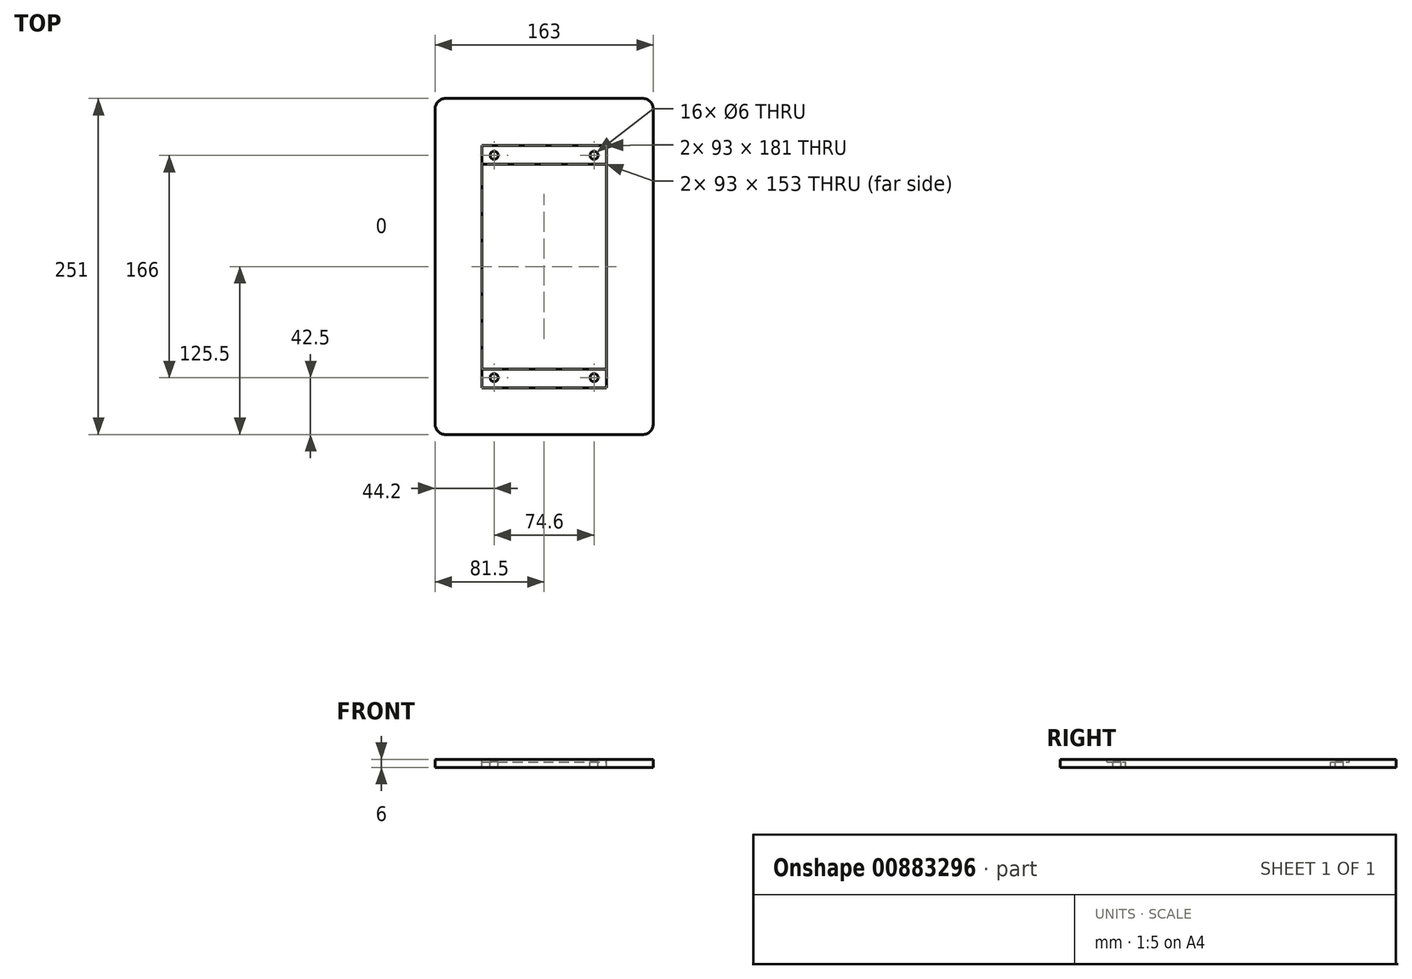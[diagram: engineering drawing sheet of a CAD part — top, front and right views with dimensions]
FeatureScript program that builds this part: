
annotation { "Feature Type Name" : "Feature", "Feature Type Description" : "" }
export const myFeature = defineFeature(function(context is Context, id is Id, definition is map)
    precondition{}
    {
        {
            var Q0;
            Q0=qCreatedBy(makeId("Top.planeOp"),FACE);
            var sketch = newSketch(context, id + "F0", { "sketchPlane" : qUnion([Q0])});
            skLineSegment(sketch, "E0.bottom", {"start": v(46.5, -76.5) * mm, "end": v(-46.5, -76.5) * mm});
            skLineSegment(sketch, "E0.top", {"start": v(46.5, 76.5) * mm, "end": v(-46.5, 76.5) * mm});
            skLineSegment(sketch, "E0.left", {"start": v(46.5, -76.5) * mm, "end": v(46.5, 76.5) * mm});
            skLineSegment(sketch, "E0.right", {"start": v(-46.5, -76.5) * mm, "end": v(-46.5, 76.5) * mm});
            skPoint(sketch, "E0.middle", {"position": v(0, 0) * mm});
            skLineSegment(sketch, "E1.bottom", {"start": v(73.5, -125.5) * mm, "end": v(-73.5, -125.5) * mm});
            skLineSegment(sketch, "E1.top", {"start": v(73.5, 125.5) * mm, "end": v(-73.5, 125.5) * mm});
            skLineSegment(sketch, "E1.left", {"start": v(81.5, -117.5) * mm, "end": v(81.5, 117.5) * mm});
            skLineSegment(sketch, "E1.right", {"start": v(-81.5, -117.5) * mm, "end": v(-81.5, 117.5) * mm});
            skPoint(sketch, "E2.visualSharp", {"position": v(-81.5, 125.5) * mm});
            skArc(sketch, "E2.filletArc", {"start": v(-73.5, 125.5) * mm, "mid": v(-79.16, 123.16) * mm, "end": v(-81.5, 117.5) * mm});
            skPoint(sketch, "E3.visualSharp", {"position": v(81.5, 125.5) * mm});
            skArc(sketch, "E3.filletArc", {"start": v(81.5, 117.5) * mm, "mid": v(79.16, 123.16) * mm, "end": v(73.5, 125.5) * mm});
            skPoint(sketch, "E4.visualSharp", {"position": v(81.5, -125.5) * mm});
            skArc(sketch, "E4.filletArc", {"start": v(73.5, -125.5) * mm, "mid": v(79.16, -123.16) * mm, "end": v(81.5, -117.5) * mm});
            skPoint(sketch, "E5.visualSharp", {"position": v(-81.5, -125.5) * mm});
            skArc(sketch, "E5.filletArc", {"start": v(-81.5, -117.5) * mm, "mid": v(-79.16, -123.16) * mm, "end": v(-73.5, -125.5) * mm});
            skSolve(sketch);
        }
        {
            var Q0;
            Q0=makeQuery(id+"F0.imprint","IMPRINT",FACE,{"disambiguationData":[TD([[makeQuery(id+"F0.imprint","IMPRINT",EDGE,{"derivedFrom":sQuery(id+"F0.wireOp",EDGE,"E0.bottom")}),-1.0]])]});
            var sketch = newSketch(context, id + "F1", { "sketchPlane" : qUnion([Q0])});
            skLineSegment(sketch, "E6.bottom", {"start": v(-46.5, 76.5) * mm, "end": v(46.5, 76.5) * mm});
            skLineSegment(sketch, "E6.top", {"start": v(-46.5, 90.5) * mm, "end": v(46.5, 90.5) * mm});
            skLineSegment(sketch, "E6.left", {"start": v(-46.5, 76.5) * mm, "end": v(-46.5, 90.5) * mm});
            skLineSegment(sketch, "E6.right", {"start": v(46.5, 76.5) * mm, "end": v(46.5, 90.5) * mm});
            skLineSegment(sketch, "E7.bottom", {"start": v(-46.5, -76.5) * mm, "end": v(46.5, -76.5) * mm});
            skLineSegment(sketch, "E7.top", {"start": v(-46.5, -90.5) * mm, "end": v(46.5, -90.5) * mm});
            skLineSegment(sketch, "E7.left", {"start": v(-46.5, -76.5) * mm, "end": v(-46.5, -90.5) * mm});
            skLineSegment(sketch, "E7.right", {"start": v(46.5, -76.5) * mm, "end": v(46.5, -90.5) * mm});
            skSolve(sketch);
        }
        {
            var Q0;
            Q0=makeQuery(id+"F0.imprint","IMPRINT",FACE,{"disambiguationData":[TD([[makeQuery(id+"F0.imprint","IMPRINT",EDGE,{"derivedFrom":sQuery(id+"F0.wireOp",EDGE,"E0.bottom")}),1.0]])]});
            extrude(context, id + "F2", {"entities" : qUnion([Q0]), "oppositeDirection" : true, "depth" : 6 * mm, "offsetDistance" : 25.4 * mm});
        }
        {
            var Q0;
            Q0 = qSketchRegion(id + "F1", true);
            var Q1;
            Q1=makeQuery(id+"F1.imprint","IMPRINT",FACE,{"disambiguationData":[TD([[makeQuery(id+"F1.imprint","IMPRINT",EDGE,{"derivedFrom":sQuery(id+"F1.wireOp",EDGE,"E6.bottom")}),1.0]])]});
            extrude(context, id + "F3", {"entities" : qUnion([Q0, Q1]), "operationType" : NewBodyOperationType.REMOVE, "oppositeDirection" : true, "depth" : 2 * mm, "offsetDistance" : 25.4 * mm});
        }
        {
            var Q0;
            Q0=makeQuery(id+"F0.imprint","IMPRINT",FACE,{"disambiguationData":[TD([[makeQuery(id+"F0.imprint","IMPRINT",EDGE,{"derivedFrom":sQuery(id+"F0.wireOp",EDGE,"E0.bottom")}),1.0]])]});
            var sketch = newSketch(context, id + "F4", { "sketchPlane" : qUnion([Q0])});
            skCircle(sketch, "E8", {"center": v(37.3, 83) * mm, "radius": 3 * mm});
            skCircle(sketch, "E9", {"center": v(-37.3, 83) * mm, "radius": 3 * mm});
            skCircle(sketch, "E10", {"center": v(37.3, -83) * mm, "radius": 3 * mm});
            skCircle(sketch, "E11", {"center": v(-37.3, -83) * mm, "radius": 3 * mm});
            skSolve(sketch);
        }
        {
            var Q0;
            Q0=sQuery(id+"F4.wireOp",VERTEX,"E9.center");
            var Q1;
            Q1=sQuery(id+"F4.wireOp",VERTEX,"E8.center");
            var Q2;
            Q2=sQuery(id+"F4.wireOp",VERTEX,"E10.center");
            var Q3;
            Q3=sQuery(id+"F4.wireOp",VERTEX,"E11.center");
            var Q4;
            Q4=makeQuery(id+"F2.opExtrude","SWEPT_BODY",BODY,{"disambiguationData":[OSD([sQuery(id+"F0.wireOp",EDGE,"E0.bottom"),sQuery(id+"F0.wireOp",EDGE,"E0.top"),sQuery(id+"F0.wireOp",EDGE,"E0.left"),sQuery(id+"F0.wireOp",EDGE,"E0.right"),sQuery(id+"F0.wireOp",EDGE,"E1.bottom"),sQuery(id+"F0.wireOp",EDGE,"E1.top"),sQuery(id+"F0.wireOp",EDGE,"E1.left"),sQuery(id+"F0.wireOp",EDGE,"E1.right"),sQuery(id+"F0.wireOp",EDGE,"E2.filletArc"),sQuery(id+"F0.wireOp",EDGE,"E3.filletArc"),sQuery(id+"F0.wireOp",EDGE,"E4.filletArc"),sQuery(id+"F0.wireOp",EDGE,"E5.filletArc")])]});
            hole(context, id + "F5", {"style" : HoleStyle.SIMPLE, "endStyle" : HoleEndStyle.THROUGH, "standardTappedOrClearance" : lookupTablePath({ "standard" : "ISO", "size" : "6", "type" : "Drilled" }), "standardBlindInLast" : lookupTablePath({ "standard" : "ISO", "size" : "6", "type" : "Drilled" }), "holeDiameter" : 6 * mm, "majorDiameter" : 6.35 * mm, "isTappedThrough" : true, "tappedDepth" : 0.5 * mm, "tapClearance" : 3, "locations" : qUnion([Q0, Q1, Q2, Q3]), "scope" : qUnion([Q4])});
        }
    });
